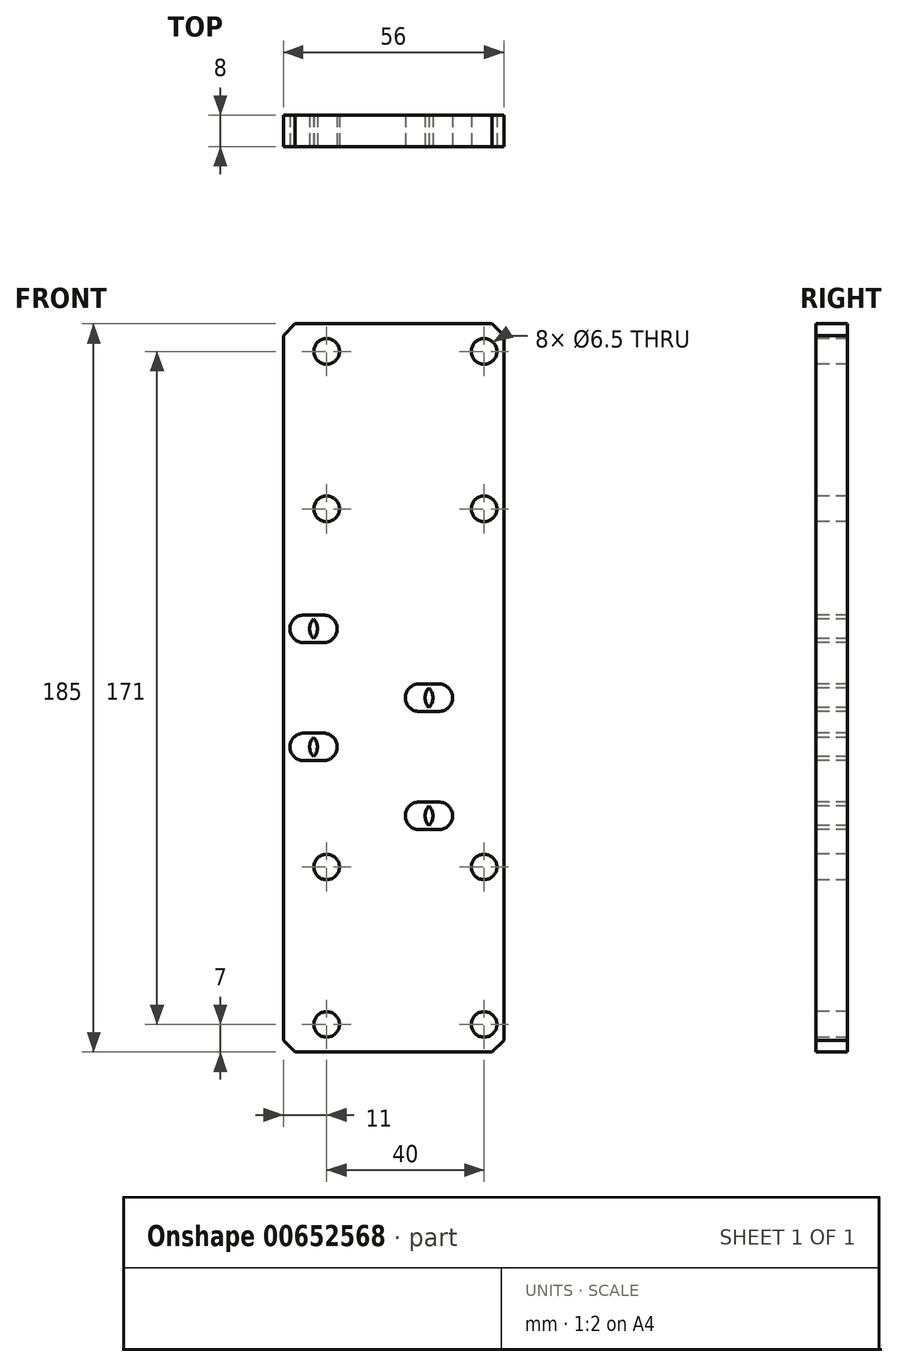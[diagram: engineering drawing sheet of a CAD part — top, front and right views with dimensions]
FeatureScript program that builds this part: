
annotation { "Feature Type Name" : "Feature", "Feature Type Description" : "" }
export const myFeature = defineFeature(function(context is Context, id is Id, definition is map)
    precondition{}
    {
        {
            var Q0;
            Q0=qCreatedBy(makeId("Front.planeOp"),FACE);
            var sketch = newSketch(context, id + "F0", { "sketchPlane" : qUnion([Q0])});
            skLineSegment(sketch, "E0.bottom", {"start": v(28, 92.5) * mm, "end": v(-28, 92.5) * mm});
            skLineSegment(sketch, "E0.top", {"start": v(28, -92.5) * mm, "end": v(-28, -92.5) * mm});
            skLineSegment(sketch, "E0.left", {"start": v(28, 92.5) * mm, "end": v(28, -92.5) * mm});
            skLineSegment(sketch, "E0.right", {"start": v(-28, 92.5) * mm, "end": v(-28, -92.5) * mm});
            skPoint(sketch, "E0.middle", {"position": v(0, 0) * mm});
            skSolve(sketch);
        }
        {
            var Q0;
            Q0 = qSketchRegion(id + "F0", true);
            extrude(context, id + "F1", {"entities" : qUnion([Q0]), "depth" : 8 * mm, "offsetDistance" : 25 * mm});
        }
        {
            var Q0;
            Q0=makeQuery(id+"F1.opExtrude","SWEPT_EDGE",EDGE,{"disambiguationData":[OSD([sQuery(id+"F0.wireOp",EDGE,"E0.bottom"),sQuery(id+"F0.wireOp",EDGE,"E0.left")])]});
            var Q1;
            Q1=makeQuery(id+"F1.opExtrude","SWEPT_EDGE",EDGE,{"disambiguationData":[OSD([sQuery(id+"F0.wireOp",EDGE,"E0.bottom"),sQuery(id+"F0.wireOp",EDGE,"E0.right")])]});
            var Q2;
            Q2=makeQuery(id+"F1.opExtrude","SWEPT_EDGE",EDGE,{"disambiguationData":[OSD([sQuery(id+"F0.wireOp",EDGE,"E0.top"),sQuery(id+"F0.wireOp",EDGE,"E0.left")])]});
            var Q3;
            Q3=makeQuery(id+"F1.opExtrude","SWEPT_EDGE",EDGE,{"disambiguationData":[OSD([sQuery(id+"F0.wireOp",EDGE,"E0.top"),sQuery(id+"F0.wireOp",EDGE,"E0.right")])]});
            chamfer(context, id + "F2", {"entities" : qUnion([Q0, Q1, Q2, Q3]), "width" : 3 * mm, "tangentPropagation" : true});
        }
        {
            var Q0;
            Q0=makeQuery(id+"F1.opExtrude","CAP_FACE",FACE,{"disambiguationData":[OSD([sQuery(id+"F0.wireOp",EDGE,"E0.bottom"),sQuery(id+"F0.wireOp",EDGE,"E0.top"),sQuery(id+"F0.wireOp",EDGE,"E0.left"),sQuery(id+"F0.wireOp",EDGE,"E0.right")])],"isStart":false});
            var sketch = newSketch(context, id + "F3", { "sketchPlane" : qUnion([Q0])});
            skPoint(sketch, "E1", {"position": v(-17, -85.5) * mm});
            skPoint(sketch, "E2", {"position": v(23, -85.5) * mm});
            skPoint(sketch, "E3", {"position": v(-17, 85.5) * mm});
            skPoint(sketch, "E4", {"position": v(23, 85.5) * mm});
            skPoint(sketch, "E5", {"position": v(-17, 45.5) * mm});
            skPoint(sketch, "E6", {"position": v(23, 45.5) * mm});
            skPoint(sketch, "E7", {"position": v(-17, -45.5) * mm});
            skPoint(sketch, "E8", {"position": v(23, -45.5) * mm});
            skSolve(sketch);
        }
        {
            var Q0;
            Q0=sQuery(id+"F3.wireOp",VERTEX,"E1");
            var Q1;
            Q1=sQuery(id+"F3.wireOp",VERTEX,"E2");
            var Q2;
            Q2=sQuery(id+"F3.wireOp",VERTEX,"E8");
            var Q3;
            Q3=sQuery(id+"F3.wireOp",VERTEX,"E7");
            var Q4;
            Q4=sQuery(id+"F3.wireOp",VERTEX,"E5");
            var Q5;
            Q5=sQuery(id+"F3.wireOp",VERTEX,"E6");
            var Q6;
            Q6=sQuery(id+"F3.wireOp",VERTEX,"E4");
            var Q7;
            Q7=sQuery(id+"F3.wireOp",VERTEX,"E3");
            var Q8;
            Q8=makeQuery(id+"F1.opExtrude","SWEPT_BODY",BODY,{"disambiguationData":[OSD([sQuery(id+"F0.wireOp",EDGE,"E0.bottom"),sQuery(id+"F0.wireOp",EDGE,"E0.top"),sQuery(id+"F0.wireOp",EDGE,"E0.left"),sQuery(id+"F0.wireOp",EDGE,"E0.right")])]});
            hole(context, id + "F4", {"style" : HoleStyle.SIMPLE, "endStyle" : HoleEndStyle.THROUGH, "holeDiameter" : 6.5 * mm, "majorDiameter" : 5 * mm, "isTappedThrough" : true, "tappedDepth" : 12 * mm, "tapClearance" : 3, "locations" : qUnion([Q0, Q1, Q2, Q3, Q4, Q5, Q6, Q7]), "scope" : qUnion([Q8])});
        }
        {
            var Q0;
            Q0=makeQuery(id+"F1.opExtrude","CAP_FACE",FACE,{"disambiguationData":[OSD([sQuery(id+"F0.wireOp",EDGE,"E0.bottom"),sQuery(id+"F0.wireOp",EDGE,"E0.top"),sQuery(id+"F0.wireOp",EDGE,"E0.left"),sQuery(id+"F0.wireOp",EDGE,"E0.right")])],"isStart":false});
            var sketch = newSketch(context, id + "F5", { "sketchPlane" : qUnion([Q0])});
            skLineSegment(sketch, "E9.bottom", {"start": v(6.5, -6) * mm, "end": v(11.5, -6) * mm});
            skLineSegment(sketch, "E9.top", {"start": v(6.5, 1) * mm, "end": v(11.5, 1) * mm});
            skLineSegment(sketch, "E9.left", {"start": v(6.5, -6) * mm, "end": v(6.5, 1) * mm});
            skLineSegment(sketch, "E9.right", {"start": v(11.5, -6) * mm, "end": v(11.5, 1) * mm});
            skPoint(sketch, "E9.middle", {"position": v(9, -2.5) * mm});
            skCircle(sketch, "E10", {"center": v(6.5, -2.5) * mm, "radius": 3.5 * mm});
            skCircle(sketch, "E11", {"center": v(11.5, -2.5) * mm, "radius": 3.5 * mm});
            skLineSegment(sketch, "E12.bottom", {"start": v(6.5, -36) * mm, "end": v(11.5, -36) * mm});
            skLineSegment(sketch, "E12.top", {"start": v(6.5, -29) * mm, "end": v(11.5, -29) * mm});
            skLineSegment(sketch, "E12.left", {"start": v(6.5, -36) * mm, "end": v(6.5, -29) * mm});
            skLineSegment(sketch, "E12.right", {"start": v(11.5, -36) * mm, "end": v(11.5, -29) * mm});
            skPoint(sketch, "E12.middle", {"position": v(9, -32.5) * mm});
            skCircle(sketch, "E13", {"center": v(6.5, -32.5) * mm, "radius": 3.5 * mm});
            skCircle(sketch, "E14", {"center": v(11.5, -32.5) * mm, "radius": 3.5 * mm});
            skLineSegment(sketch, "E15.bottom", {"start": v(-22.8, -18.5) * mm, "end": v(-17.81, -18.5) * mm});
            skLineSegment(sketch, "E15.top", {"start": v(-22.8, -11.5) * mm, "end": v(-17.81, -11.5) * mm});
            skLineSegment(sketch, "E15.left", {"start": v(-22.81, -18.5) * mm, "end": v(-22.8, -11.5) * mm});
            skLineSegment(sketch, "E15.right", {"start": v(-17.81, -18.5) * mm, "end": v(-17.81, -11.5) * mm});
            skPoint(sketch, "E15.middle", {"position": v(-20.31, -15) * mm});
            skCircle(sketch, "E16", {"center": v(-22.81, -15) * mm, "radius": 3.5 * mm});
            skCircle(sketch, "E17", {"center": v(-17.81, -15) * mm, "radius": 3.5 * mm});
            skLineSegment(sketch, "E18.bottom", {"start": v(-22.81, 11.5) * mm, "end": v(-17.81, 11.5) * mm});
            skLineSegment(sketch, "E18.top", {"start": v(-22.81, 18.5) * mm, "end": v(-17.81, 18.5) * mm});
            skLineSegment(sketch, "E18.left", {"start": v(-22.81, 11.5) * mm, "end": v(-22.81, 18.5) * mm});
            skLineSegment(sketch, "E18.right", {"start": v(-17.81, 11.5) * mm, "end": v(-17.81, 18.5) * mm});
            skPoint(sketch, "E18.middle", {"position": v(-20.31, 15) * mm});
            skCircle(sketch, "E19", {"center": v(-22.81, 15) * mm, "radius": 3.5 * mm});
            skCircle(sketch, "E20", {"center": v(-17.81, 15) * mm, "radius": 3.5 * mm});
            skSolve(sketch);
        }
        {
            var Q0;
            {var subQ0=sQuery(id+"F5.wireOp",EDGE,"E9.left");Q0=makeQuery(id+"F5.imprint","IMPRINT",FACE,{"disambiguationData":[TD([[makeQuery(id+"F5.imprint","IMPRINT",EDGE,{"derivedFrom":subQ0}),1.0]])]});}
            var Q1;
            {var subQ0=sQuery(id+"F5.wireOp",EDGE,"E9.right");Q1=makeQuery(id+"F5.imprint","IMPRINT",FACE,{"disambiguationData":[TD([[makeQuery(id+"F5.imprint","IMPRINT",EDGE,{"derivedFrom":subQ0}),-1.0]])]});}
            var Q2;
            {var subQ0=sQuery(id+"F5.wireOp",EDGE,"E12.left");Q2=makeQuery(id+"F5.imprint","IMPRINT",FACE,{"disambiguationData":[TD([[makeQuery(id+"F5.imprint","IMPRINT",EDGE,{"derivedFrom":subQ0}),1.0]])]});}
            var Q3;
            {var subQ0=sQuery(id+"F5.wireOp",EDGE,"E12.right");Q3=makeQuery(id+"F5.imprint","IMPRINT",FACE,{"disambiguationData":[TD([[makeQuery(id+"F5.imprint","IMPRINT",EDGE,{"derivedFrom":subQ0}),-1.0]])]});}
            var Q4;
            {var subQ0=sQuery(id+"F5.wireOp",EDGE,"E15.right");Q4=makeQuery(id+"F5.imprint","IMPRINT",FACE,{"disambiguationData":[TD([[makeQuery(id+"F5.imprint","IMPRINT",EDGE,{"derivedFrom":subQ0}),-1.0]])]});}
            var Q5;
            {var subQ0=sQuery(id+"F5.wireOp",EDGE,"E18.left");Q5=makeQuery(id+"F5.imprint","IMPRINT",FACE,{"disambiguationData":[TD([[makeQuery(id+"F5.imprint","IMPRINT",EDGE,{"derivedFrom":subQ0}),1.0]])]});}
            var Q6;
            {var subQ0=sQuery(id+"F5.wireOp",EDGE,"E18.right");Q6=makeQuery(id+"F5.imprint","IMPRINT",FACE,{"disambiguationData":[TD([[makeQuery(id+"F5.imprint","IMPRINT",EDGE,{"derivedFrom":subQ0}),-1.0]])]});}
            var Q7;
            {var subQ0=sQuery(id+"F5.wireOp",EDGE,"E9.bottom");Q7=makeQuery(id+"F5.imprint","IMPRINT",FACE,{"disambiguationData":[TD([[makeQuery(id+"F5.imprint","IMPRINT",EDGE,{"derivedFrom":subQ0}),1.0]])]});}
            var Q8;
            {var subQ0=sQuery(id+"F5.wireOp",EDGE,"E9.top");Q8=makeQuery(id+"F5.imprint","IMPRINT",FACE,{"disambiguationData":[TD([[makeQuery(id+"F5.imprint","IMPRINT",EDGE,{"derivedFrom":subQ0}),-1.0]])]});}
            var Q9;
            {var subQ0=sQuery(id+"F5.wireOp",EDGE,"E12.bottom");Q9=makeQuery(id+"F5.imprint","IMPRINT",FACE,{"disambiguationData":[TD([[makeQuery(id+"F5.imprint","IMPRINT",EDGE,{"derivedFrom":subQ0}),1.0]])]});}
            var Q10;
            {var subQ0=sQuery(id+"F5.wireOp",EDGE,"E12.top");Q10=makeQuery(id+"F5.imprint","IMPRINT",FACE,{"disambiguationData":[TD([[makeQuery(id+"F5.imprint","IMPRINT",EDGE,{"derivedFrom":subQ0}),-1.0]])]});}
            var Q11;
            {var subQ0=sQuery(id+"F5.wireOp",EDGE,"E15.bottom");Q11=makeQuery(id+"F5.imprint","IMPRINT",FACE,{"disambiguationData":[TD([[makeQuery(id+"F5.imprint","IMPRINT",EDGE,{"derivedFrom":subQ0}),1.0]])]});}
            var Q12;
            {var subQ0=sQuery(id+"F5.wireOp",EDGE,"E15.top");Q12=makeQuery(id+"F5.imprint","IMPRINT",FACE,{"disambiguationData":[TD([[makeQuery(id+"F5.imprint","IMPRINT",EDGE,{"derivedFrom":subQ0}),-1.0]])]});}
            var Q13;
            {var subQ0=sQuery(id+"F5.wireOp",EDGE,"E18.bottom");Q13=makeQuery(id+"F5.imprint","IMPRINT",FACE,{"disambiguationData":[TD([[makeQuery(id+"F5.imprint","IMPRINT",EDGE,{"derivedFrom":subQ0}),1.0]])]});}
            var Q14;
            {var subQ0=sQuery(id+"F5.wireOp",EDGE,"E18.top");Q14=makeQuery(id+"F5.imprint","IMPRINT",FACE,{"disambiguationData":[TD([[makeQuery(id+"F5.imprint","IMPRINT",EDGE,{"derivedFrom":subQ0}),-1.0]])]});}
            var Q15;
            {var subQ0=sQuery(id+"F5.wireOp",EDGE,"E9.left");Q15=makeQuery(id+"F5.imprint","IMPRINT",FACE,{"disambiguationData":[TD([[makeQuery(id+"F5.imprint","IMPRINT",EDGE,{"derivedFrom":subQ0}),-1.0]])]});}
            var Q16;
            {var subQ0=sQuery(id+"F5.wireOp",EDGE,"E9.right");Q16=makeQuery(id+"F5.imprint","IMPRINT",FACE,{"disambiguationData":[TD([[makeQuery(id+"F5.imprint","IMPRINT",EDGE,{"derivedFrom":subQ0}),1.0]])]});}
            var Q17;
            {var subQ0=sQuery(id+"F5.wireOp",EDGE,"E12.left");Q17=makeQuery(id+"F5.imprint","IMPRINT",FACE,{"disambiguationData":[TD([[makeQuery(id+"F5.imprint","IMPRINT",EDGE,{"derivedFrom":subQ0}),-1.0]])]});}
            var Q18;
            {var subQ0=sQuery(id+"F5.wireOp",EDGE,"E12.right");Q18=makeQuery(id+"F5.imprint","IMPRINT",FACE,{"disambiguationData":[TD([[makeQuery(id+"F5.imprint","IMPRINT",EDGE,{"derivedFrom":subQ0}),1.0]])]});}
            var Q19;
            {var subQ0=sQuery(id+"F5.wireOp",EDGE,"E15.left");Q19=makeQuery(id+"F5.imprint","IMPRINT",FACE,{"disambiguationData":[TD([[makeQuery(id+"F5.imprint","IMPRINT",EDGE,{"derivedFrom":subQ0}),-1.0]])]});}
            var Q20;
            {var subQ0=sQuery(id+"F5.wireOp",EDGE,"E15.right");Q20=makeQuery(id+"F5.imprint","IMPRINT",FACE,{"disambiguationData":[TD([[makeQuery(id+"F5.imprint","IMPRINT",EDGE,{"derivedFrom":subQ0}),1.0]])]});}
            var Q21;
            {var subQ0=sQuery(id+"F5.wireOp",EDGE,"E18.left");Q21=makeQuery(id+"F5.imprint","IMPRINT",FACE,{"disambiguationData":[TD([[makeQuery(id+"F5.imprint","IMPRINT",EDGE,{"derivedFrom":subQ0}),-1.0]])]});}
            var Q22;
            {var subQ0=sQuery(id+"F5.wireOp",EDGE,"E18.right");Q22=makeQuery(id+"F5.imprint","IMPRINT",FACE,{"disambiguationData":[TD([[makeQuery(id+"F5.imprint","IMPRINT",EDGE,{"derivedFrom":subQ0}),1.0]])]});}
            var Q23;
            {var subQ0=sQuery(id+"F5.wireOp",EDGE,"E15.left");Q23=makeQuery(id+"F5.imprint","IMPRINT",FACE,{"disambiguationData":[TD([[makeQuery(id+"F5.imprint","IMPRINT",EDGE,{"derivedFrom":subQ0}),1.0]])]});}
            var Q24;
            {var subQ0=sQuery(id+"F5.wireOp",EDGE,"E17");var subQ1=sQuery(id+"F5.wireOp",EDGE,"E16");var subQ2=makeQuery(id+"F5.imprint","INTERSECT",VERTEX,{"disambiguationData":[OD(0.0)],"derivedFrom":[subQ1,subQ0]});Q24=makeQuery(id+"F5.imprint","IMPRINT",FACE,{"disambiguationData":[TD([[makeQuery(id+"F5.imprint","IMPRINT",EDGE,{"disambiguationData":[TD([[subQ2,1.0]])],"derivedFrom":subQ1}),1.0]])]});}
            var Q25;
            {var subQ0=sQuery(id+"F5.wireOp",EDGE,"E20");var subQ1=sQuery(id+"F5.wireOp",EDGE,"E19");var subQ2=makeQuery(id+"F5.imprint","INTERSECT",VERTEX,{"disambiguationData":[OD(0.0)],"derivedFrom":[subQ1,subQ0]});Q25=makeQuery(id+"F5.imprint","IMPRINT",FACE,{"disambiguationData":[TD([[makeQuery(id+"F5.imprint","IMPRINT",EDGE,{"disambiguationData":[TD([[subQ2,1.0]])],"derivedFrom":subQ1}),1.0]])]});}
            var Q26;
            {var subQ0=sQuery(id+"F5.wireOp",EDGE,"E11");var subQ1=sQuery(id+"F5.wireOp",EDGE,"E10");var subQ2=makeQuery(id+"F5.imprint","INTERSECT",VERTEX,{"disambiguationData":[OD(0.0)],"derivedFrom":[subQ1,subQ0]});Q26=makeQuery(id+"F5.imprint","IMPRINT",FACE,{"disambiguationData":[TD([[makeQuery(id+"F5.imprint","IMPRINT",EDGE,{"disambiguationData":[TD([[subQ2,1.0]])],"derivedFrom":subQ1}),1.0]])]});}
            var Q27;
            {var subQ0=sQuery(id+"F5.wireOp",EDGE,"E14");var subQ1=sQuery(id+"F5.wireOp",EDGE,"E13");var subQ2=makeQuery(id+"F5.imprint","INTERSECT",VERTEX,{"disambiguationData":[OD(0.0)],"derivedFrom":[subQ1,subQ0]});Q27=makeQuery(id+"F5.imprint","IMPRINT",FACE,{"disambiguationData":[TD([[makeQuery(id+"F5.imprint","IMPRINT",EDGE,{"disambiguationData":[TD([[subQ2,1.0]])],"derivedFrom":subQ1}),1.0]])]});}
            extrude(context, id + "F6", {"entities" : qUnion([Q0, Q1, Q2, Q3, Q4, Q5, Q6, Q7, Q8, Q9, Q10, Q11, Q12, Q13, Q14, Q15, Q16, Q17, Q18, Q19, Q20, Q21, Q22, Q23, Q24, Q25, Q26, Q27]), "operationType" : NewBodyOperationType.REMOVE, "oppositeDirection" : true, "depth" : 25 * mm, "offsetDistance" : 25 * mm});
        }
    });
